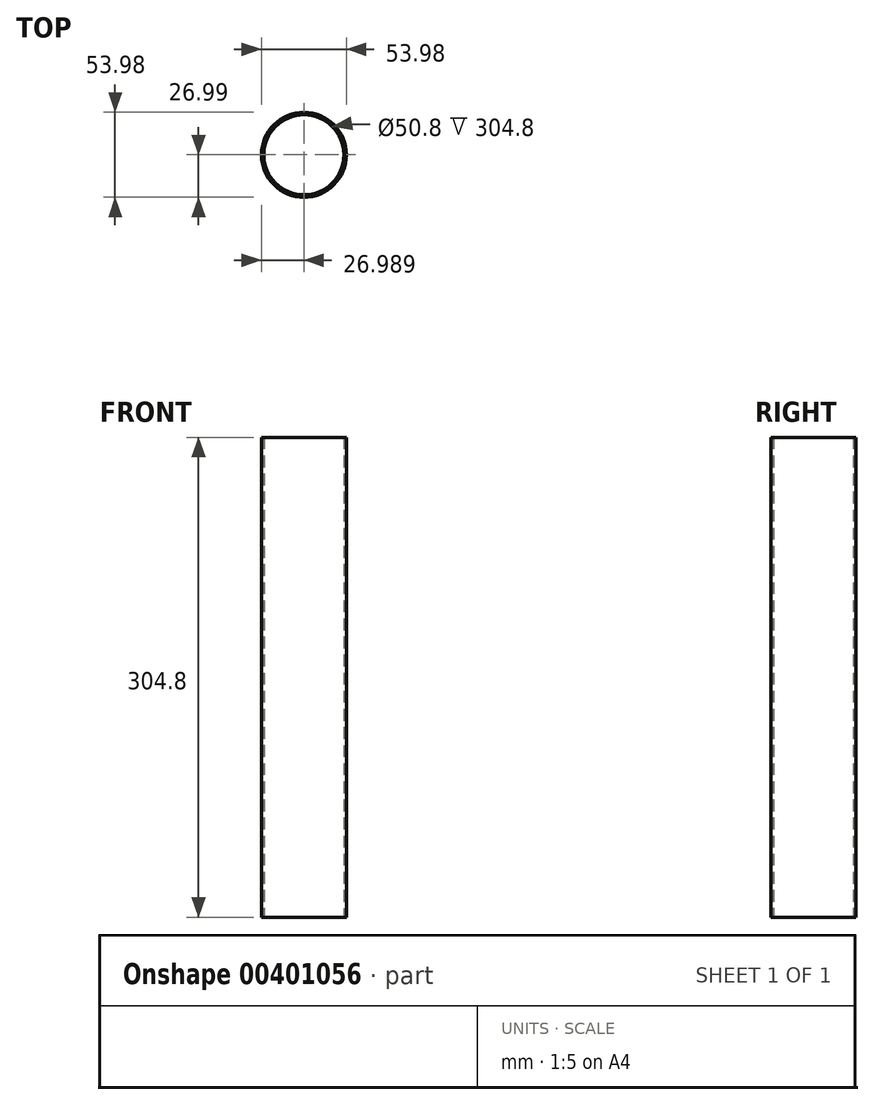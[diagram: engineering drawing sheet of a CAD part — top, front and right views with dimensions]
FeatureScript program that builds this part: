
annotation { "Feature Type Name" : "Feature", "Feature Type Description" : "" }
export const myFeature = defineFeature(function(context is Context, id is Id, definition is map)
    precondition{}
    {
        {
            var Q0;
            Q0=qCreatedBy(makeId("Top.planeOp"),FACE);
            var sketch = newSketch(context, id + "F0", { "sketchPlane" : qUnion([Q0])});
            skCircle(sketch, "E0", {"center": v(0.82, 0) * mm, "radius": 25.4 * mm});
            skCircle(sketch, "E1.0", {"center": v(0.82, 0) * mm, "radius": 26.99 * mm});
            skSolve(sketch);
        }
        {
            var Q0;
            Q0=makeQuery(id+"F0.imprint","IMPRINT",FACE,{"disambiguationData":[TD([[makeQuery(id+"F0.imprint","IMPRINT",EDGE,{"derivedFrom":sQuery(id+"F0.wireOp",EDGE,"E0")}),-1.0]])]});
            extrude(context, id + "F1", {"entities" : qUnion([Q0]), "depth" : 304.8 * mm});
        }
    });
